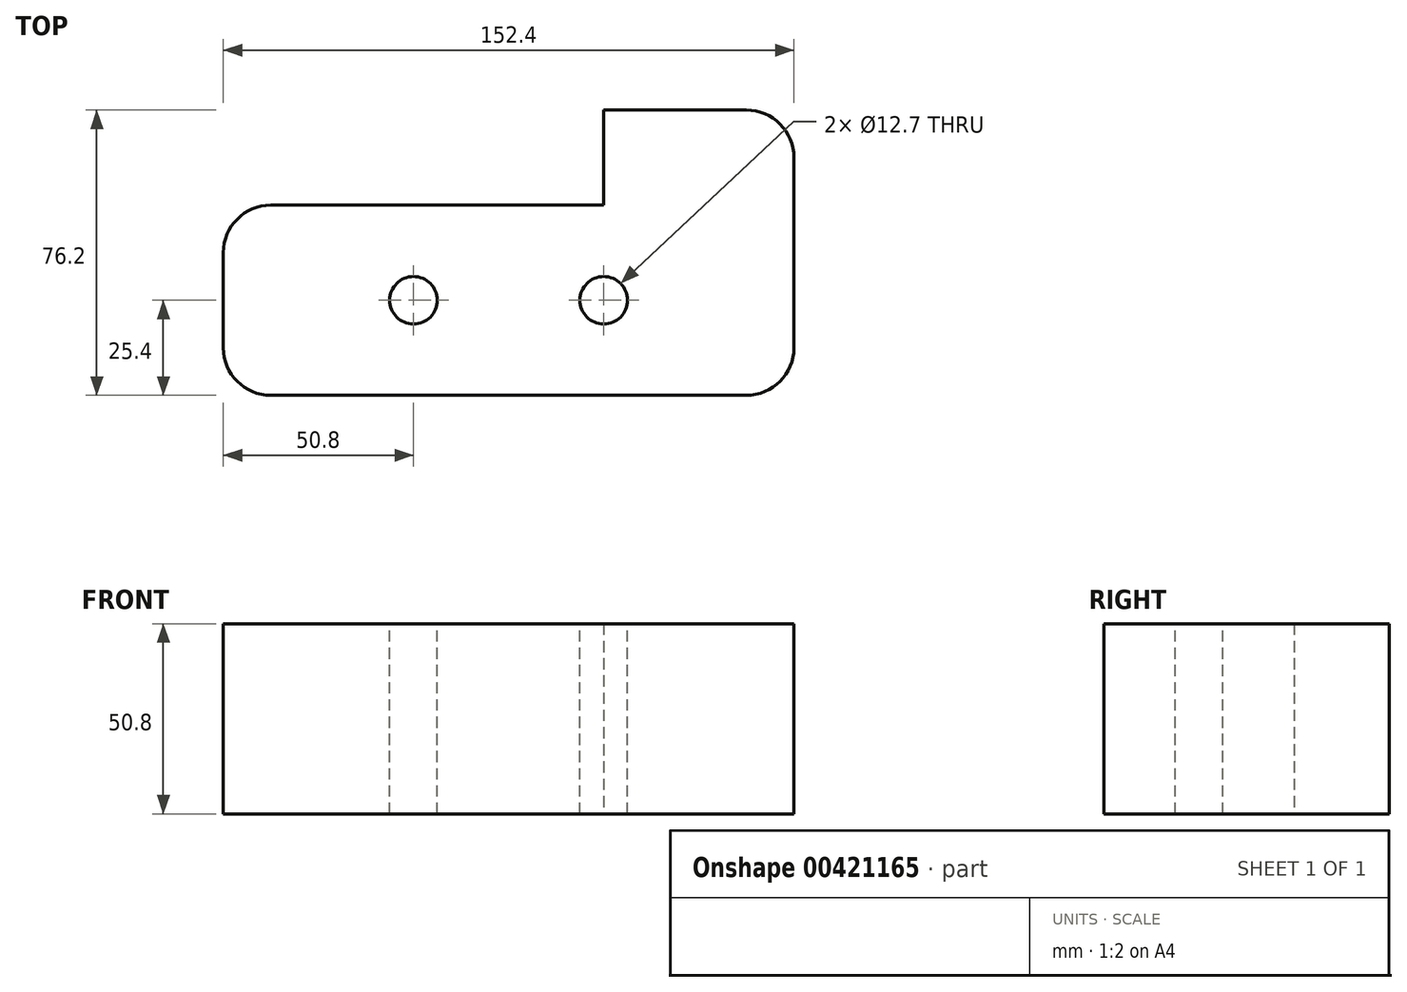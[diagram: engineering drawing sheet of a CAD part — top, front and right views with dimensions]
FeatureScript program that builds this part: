
annotation { "Feature Type Name" : "Feature", "Feature Type Description" : "" }
export const myFeature = defineFeature(function(context is Context, id is Id, definition is map)
    precondition{}
    {
        {
            var Q0;
            Q0=qCreatedBy(makeId("Top.planeOp"),FACE);
            var sketch = newSketch(context, id + "F0", { "sketchPlane" : qUnion([Q0])});
            skLineSegment(sketch, "E0", {"start": v(12.7, 0) * mm, "end": v(139.7, 0) * mm});
            skLineSegment(sketch, "E1", {"start": v(0, 12.7) * mm, "end": v(0, 38.1) * mm});
            skLineSegment(sketch, "E2", {"start": v(12.7, 50.8) * mm, "end": v(101.6, 50.8) * mm});
            skLineSegment(sketch, "E3", {"start": v(101.6, 50.8) * mm, "end": v(101.6, 76.2) * mm});
            skLineSegment(sketch, "E4", {"start": v(101.6, 76.2) * mm, "end": v(139.7, 76.2) * mm});
            skLineSegment(sketch, "E5", {"start": v(152.4, 63.5) * mm, "end": v(152.4, 12.7) * mm});
            skPoint(sketch, "E6.visualSharp", {"position": v(152.4, 76.2) * mm});
            skArc(sketch, "E6.filletArc", {"start": v(152.4, 63.5) * mm, "mid": v(148.68, 72.48) * mm, "end": v(139.7, 76.2) * mm});
            skPoint(sketch, "E7.visualSharp", {"position": v(152.4, 0) * mm});
            skArc(sketch, "E7.filletArc", {"start": v(139.7, 0) * mm, "mid": v(148.68, 3.72) * mm, "end": v(152.4, 12.7) * mm});
            skPoint(sketch, "E8.visualSharp", {"position": v(0, 0) * mm});
            skArc(sketch, "E8.filletArc", {"start": v(0, 12.7) * mm, "mid": v(3.72, 3.72) * mm, "end": v(12.7, 0) * mm});
            skPoint(sketch, "E9.visualSharp", {"position": v(0, 50.8) * mm});
            skArc(sketch, "E9.filletArc", {"start": v(12.7, 50.8) * mm, "mid": v(3.72, 47.08) * mm, "end": v(0, 38.1) * mm});
            skSolve(sketch);
        }
        {
            var Q0;
            Q0=makeQuery(id+"F0.imprint","IMPRINT",FACE,{"disambiguationData":[TD([[makeQuery(id+"F0.imprint","IMPRINT",EDGE,{"derivedFrom":sQuery(id+"F0.wireOp",EDGE,"E0")}),1.0]])]});
            extrude(context, id + "F1", {"entities" : qUnion([Q0]), "depth" : 50.8 * mm});
        }
        {
            var Q0;
            Q0=makeQuery(id+"F1.opExtrude","CAP_FACE",FACE,{"disambiguationData":[OSD([sQuery(id+"F0.wireOp",EDGE,"E0"),sQuery(id+"F0.wireOp",EDGE,"E1"),sQuery(id+"F0.wireOp",EDGE,"E2"),sQuery(id+"F0.wireOp",EDGE,"E3"),sQuery(id+"F0.wireOp",EDGE,"E4"),sQuery(id+"F0.wireOp",EDGE,"E5"),sQuery(id+"F0.wireOp",EDGE,"E6.filletArc"),sQuery(id+"F0.wireOp",EDGE,"E7.filletArc"),sQuery(id+"F0.wireOp",EDGE,"E8.filletArc"),sQuery(id+"F0.wireOp",EDGE,"E9.filletArc")])],"isStart":false});
            var sketch = newSketch(context, id + "F2", { "sketchPlane" : qUnion([Q0])});
            skPoint(sketch, "E10", {"position": v(57.15, 50.8) * mm});
            skPoint(sketch, "E11", {"position": v(0, 25.4) * mm});
            skPoint(sketch, "E12", {"position": v(50.8, 25.4) * mm});
            skPoint(sketch, "E13", {"position": v(101.6, 25.4) * mm});
            skSolve(sketch);
        }
        {
            var Q0;
            Q0=sQuery(id+"F2.wireOp",VERTEX,"E12");
            var Q1;
            Q1=sQuery(id+"F2.wireOp",VERTEX,"E13");
            var Q2;
            Q2=makeQuery(id+"F1.opExtrude","SWEPT_BODY",BODY,{"disambiguationData":[OSD([sQuery(id+"F0.wireOp",EDGE,"E0"),sQuery(id+"F0.wireOp",EDGE,"E1"),sQuery(id+"F0.wireOp",EDGE,"E2"),sQuery(id+"F0.wireOp",EDGE,"E3"),sQuery(id+"F0.wireOp",EDGE,"E4"),sQuery(id+"F0.wireOp",EDGE,"E5"),sQuery(id+"F0.wireOp",EDGE,"E6.filletArc"),sQuery(id+"F0.wireOp",EDGE,"E7.filletArc"),sQuery(id+"F0.wireOp",EDGE,"E8.filletArc"),sQuery(id+"F0.wireOp",EDGE,"E9.filletArc")])]});
            hole(context, id + "F3", {"style" : HoleStyle.SIMPLE, "endStyle" : HoleEndStyle.THROUGH, "holeDiameter" : 12.7 * mm, "isTappedThrough" : true, "tappedDepth" : 12.7 * mm, "tapClearance" : 3, "locations" : qUnion([Q0, Q1]), "scope" : qUnion([Q2])});
        }
    });
